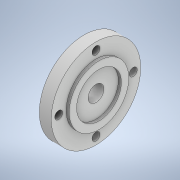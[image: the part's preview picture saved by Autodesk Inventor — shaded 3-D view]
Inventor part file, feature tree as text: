
AUTODESK INVENTOR PART (.ipt)
format: ipt  version: 2021 (Build 250183000, 183)  size: 145,920 bytes
history: native  units: mm
features: extrude x4, sketch x4
ambient origin geometry x8: Origin, YZ Plane, XZ Plane, XY Plane, X Axis, Y Axis, Z Axis, Center Point
bodies: Solid1 (feature_tree)
feature tree (8):
  extrude  "Extrusion1"  Depth=12.0mm TaperAngle=0.0deg
  extrude  "Extrusion2"  Depth=45.0mm
  extrude  "Extrusion3"  Depth=3.0mm
  extrude  "Extrusion4"  Depth=8.0mm
  sketch  "Sketch1"  dims[d0=90.0mm d1=12.0mm d2=0.0mm]
  sketch  "Sketch2"  dims[d3=60.0mm d4=45.0mm]
  sketch  "Sketch3"  dims[d5=3.0mm d6=0.0mm d7=38.0mm]
  sketch  "Sketch4"  dims[d8=3.0mm d9=0.0mm d10=16.0mm d11=8.0mm d12=37.5mm d13=40.0mm d15=360.0deg d17=75.0mm d18=37.5mm d19=0.0mm d20=0.0mm]
